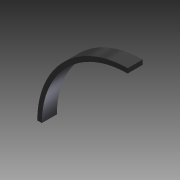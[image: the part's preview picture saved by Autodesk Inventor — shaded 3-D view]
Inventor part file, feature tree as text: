
AUTODESK INVENTOR PART (.ipt)
format: ipt  version: 2013 (Build 170138000, 138)  size: 73,216 bytes
history: native  units: in
note: dims shown in document units (in); Inventor stores cm internally (conversion verified against a paired STEP export)
features: extrude x1, sketch x1
ambient origin geometry x8: Origin, YZ Plane, XZ Plane, XY Plane, X Axis, Y Axis, Z Axis, Center Point
bodies: Solid1 (feature_tree)
feature tree (2):
  extrude  "Extrusion1"  Depth=0.75in
  sketch  "Sketch1"  dims[d0=30.0in d1=0.75in d2=2.5in d3=0.0in]
